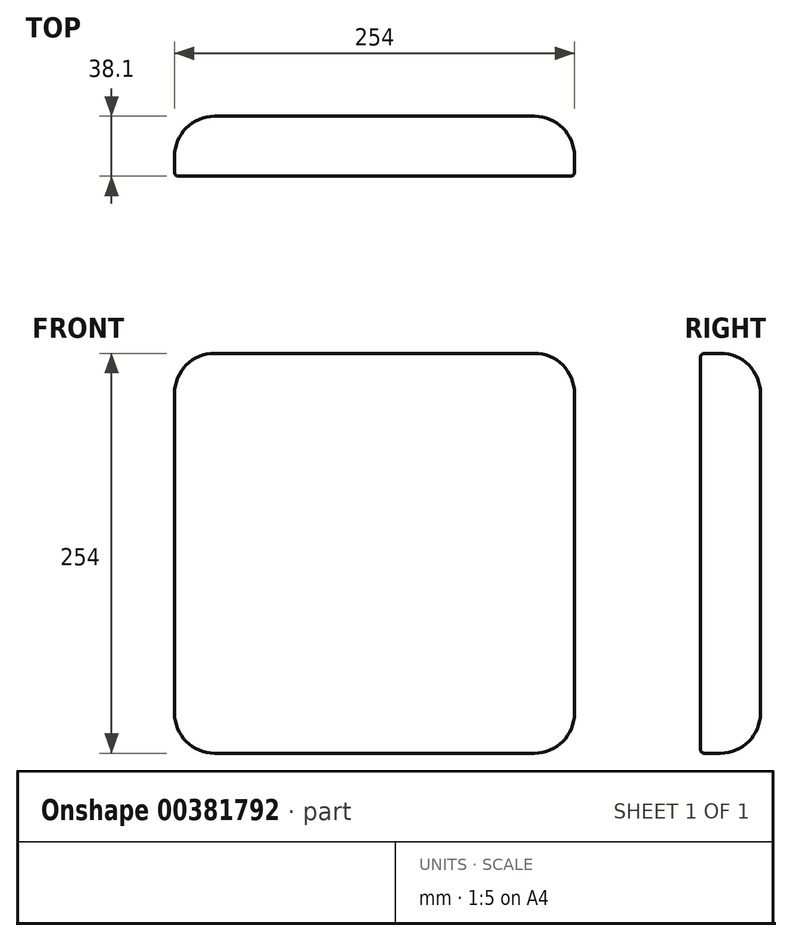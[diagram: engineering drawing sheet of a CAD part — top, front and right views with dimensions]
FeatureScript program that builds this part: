
annotation { "Feature Type Name" : "Feature", "Feature Type Description" : "" }
export const myFeature = defineFeature(function(context is Context, id is Id, definition is map)
    precondition{}
    {
        {
            var Q0;
            Q0=qCreatedBy(makeId("Front.planeOp"),FACE);
            var sketch = newSketch(context, id + "F0", { "sketchPlane" : qUnion([Q0])});
            skLineSegment(sketch, "E0.bottom", {"start": v(0, 0) * mm, "end": v(254, 0) * mm});
            skLineSegment(sketch, "E0.top", {"start": v(0, 254) * mm, "end": v(254, 254) * mm});
            skLineSegment(sketch, "E0.left", {"start": v(0, 0) * mm, "end": v(0, 254) * mm});
            skLineSegment(sketch, "E0.right", {"start": v(254, 0) * mm, "end": v(254, 254) * mm});
            skSolve(sketch);
        }
        {
            var Q0;
            Q0=makeQuery(id+"F0.imprint","IMPRINT",FACE,{"disambiguationData":[TD([[makeQuery(id+"F0.imprint","IMPRINT",EDGE,{"derivedFrom":sQuery(id+"F0.wireOp",EDGE,"E0.bottom")}),1.0]])]});
            extrude(context, id + "F1", {"entities" : qUnion([Q0]), "depth" : 38.1 * mm});
        }
        {
            var Q0;
            Q0=makeQuery(id+"F1.opExtrude","SWEPT_EDGE",EDGE,{"disambiguationData":[OSD([sQuery(id+"F0.wireOp",EDGE,"E0.top"),sQuery(id+"F0.wireOp",EDGE,"E0.left")])]});
            fillet(context, id + "F2", {"entities" : qUnion([Q0]), "radius" : 25.4 * mm, "tangentPropagation" : true, "allowEdgeOverflow" : false});
        }
        {
            var Q0;
            Q0=makeQuery(id+"F1.opExtrude","SWEPT_EDGE",EDGE,{"disambiguationData":[OSD([sQuery(id+"F0.wireOp",EDGE,"E0.bottom"),sQuery(id+"F0.wireOp",EDGE,"E0.left")])]});
            fillet(context, id + "F3", {"entities" : qUnion([Q0]), "radius" : 25.4 * mm, "tangentPropagation" : true, "allowEdgeOverflow" : false});
        }
        {
            var Q0;
            Q0=makeQuery(id+"F1.opExtrude","SWEPT_EDGE",EDGE,{"disambiguationData":[OSD([sQuery(id+"F0.wireOp",EDGE,"E0.bottom"),sQuery(id+"F0.wireOp",EDGE,"E0.right")])]});
            fillet(context, id + "F4", {"entities" : qUnion([Q0]), "radius" : 25.4 * mm, "tangentPropagation" : true, "allowEdgeOverflow" : false});
        }
        {
            var Q0;
            Q0=makeQuery(id+"F1.opExtrude","SWEPT_EDGE",EDGE,{"disambiguationData":[OSD([sQuery(id+"F0.wireOp",EDGE,"E0.top"),sQuery(id+"F0.wireOp",EDGE,"E0.right")])]});
            fillet(context, id + "F5", {"entities" : qUnion([Q0]), "radius" : 25.4 * mm, "tangentPropagation" : true, "allowEdgeOverflow" : false});
        }
        {
            var Q0;
            Q0=makeQuery(id+"F1.opExtrude","CAP_EDGE",EDGE,{"disambiguationData":[OSD([sQuery(id+"F0.wireOp",EDGE,"E0.right")])],"isStart":false});
            fillet(context, id + "F6", {"entities" : qUnion([Q0]), "radius" : 2.54 * mm, "tangentPropagation" : true, "allowEdgeOverflow" : false});
        }
        {
            var Q0;
            Q0=makeQuery(id+"F1.opExtrude","CAP_EDGE",EDGE,{"disambiguationData":[OSD([sQuery(id+"F0.wireOp",EDGE,"E0.right")])],"isStart":true});
            fillet(context, id + "F7", {"entities" : qUnion([Q0]), "radius" : 25.4 * mm, "tangentPropagation" : true, "allowEdgeOverflow" : false});
        }
    });
